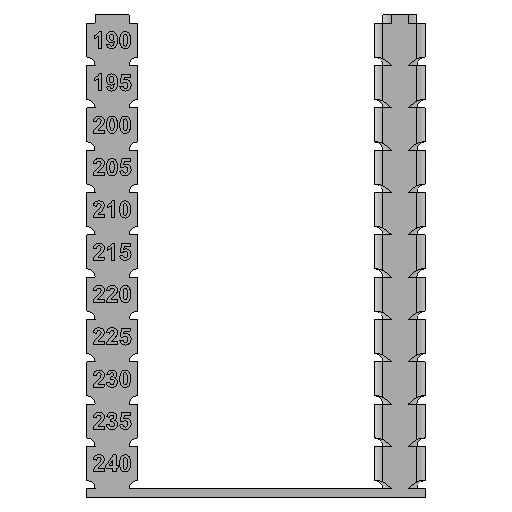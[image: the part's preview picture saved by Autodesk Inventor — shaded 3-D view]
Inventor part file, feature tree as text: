
AUTODESK INVENTOR PART (.ipt)
format: ipt  version: 2025.3 (Build 293356000, 356)  size: 1,700,352 bytes
history: native  units: mm
features: other x8, extrude x4, sketch x2, mirror x2, fillet x2, pattern_linear x2
ambient origin geometry x8: Origin, YZ Plane, XZ Plane, XY Plane, X Axis, Y Axis, Z Axis, Center Point
bodies: Body1 (feature_tree)
feature tree (20):
  other  "實體1"
  other  "temp_tower"
  sketch  "草圖1"
  extrude  "擠出1"  Depth=40.0mm
  extrude  "擠出2"  Depth=5.0mm
  mirror  "鏡射1"
  extrude  "擠出3"  Depth=6.0mm
  extrude  "擠出4"  Depth=1.0mm
  mirror  "鏡射2"
  fillet  "圓角1"  Radius=1.0mm
  pattern_linear  "矩形陣列1"  Spacing1=4.0mm  [1 undecoded]
  other  "合併1"
  fillet  "圓角2"  Radius=1.0mm
  pattern_linear  "矩形陣列2"  Spacing1=1.0mm  [1 undecoded]
  other  "浮雕1"
  other  "實體2"
  other  "陣列 實體2:1"
  other  "實體3"
  sketch  "草圖2"
  other  "MeshFeature1"
note: 2 required parameter values undecoded (feature->parameter linkage not recoverable at this tier; creation-order binding heuristic only, values carry confidence <= 0.55)
